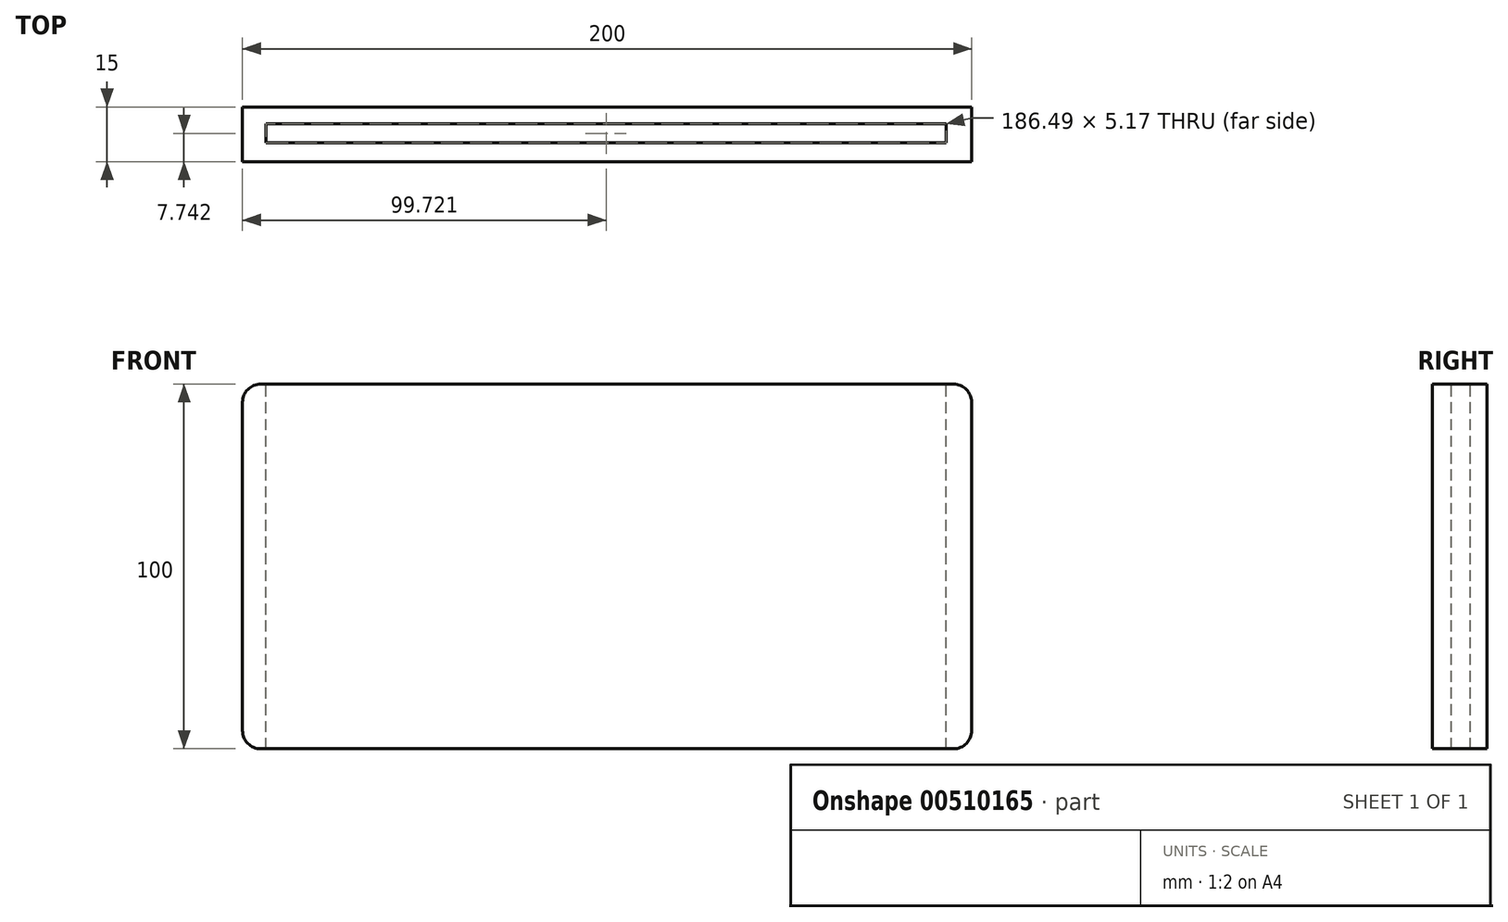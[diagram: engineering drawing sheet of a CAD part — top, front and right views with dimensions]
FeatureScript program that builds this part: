
annotation { "Feature Type Name" : "Feature", "Feature Type Description" : "" }
export const myFeature = defineFeature(function(context is Context, id is Id, definition is map)
    precondition{}
    {
        {
            var Q0;
            Q0=qCreatedBy(makeId("Front.planeOp"),FACE);
            var sketch = newSketch(context, id + "F0", { "sketchPlane" : qUnion([Q0])});
            skLineSegment(sketch, "E0.bottom", {"start": v(-99.03, -37.98) * mm, "end": v(100.97, -37.98) * mm});
            skLineSegment(sketch, "E0.top", {"start": v(-99.03, 62.02) * mm, "end": v(100.97, 62.02) * mm});
            skLineSegment(sketch, "E0.left", {"start": v(-99.03, -37.98) * mm, "end": v(-99.03, 62.02) * mm});
            skLineSegment(sketch, "E0.right", {"start": v(100.97, -37.98) * mm, "end": v(100.97, 62.02) * mm});
            skSolve(sketch);
        }
        {
            var Q0;
            Q0=makeQuery(id+"F0.imprint","IMPRINT",FACE,{"disambiguationData":[TD([[makeQuery(id+"F0.imprint","IMPRINT",EDGE,{"derivedFrom":sQuery(id+"F0.wireOp",EDGE,"E0.bottom")}),1.0]])]});
            extrude(context, id + "F1", {"entities" : qUnion([Q0]), "depth" : 15 * mm});
        }
        {
            var Q0;
            Q0=makeQuery(id+"F1.opExtrude","SWEPT_FACE",FACE,{"disambiguationData":[OSD([sQuery(id+"F0.wireOp",EDGE,"E0.bottom")])]});
            var sketch = newSketch(context, id + "F2", { "sketchPlane" : qUnion([Q0])});
            skLineSegment(sketch, "E1.bottom", {"start": v(-92.56, 9.84) * mm, "end": v(93.94, 9.84) * mm});
            skLineSegment(sketch, "E1.top", {"start": v(-92.56, 4.67) * mm, "end": v(93.94, 4.67) * mm});
            skLineSegment(sketch, "E1.left", {"start": v(-92.56, 9.84) * mm, "end": v(-92.56, 4.67) * mm});
            skLineSegment(sketch, "E1.right", {"start": v(93.94, 9.84) * mm, "end": v(93.94, 4.67) * mm});
            skSolve(sketch);
        }
        {
            var Q0;
            Q0=makeQuery(id+"F2.imprint","IMPRINT",FACE,{"disambiguationData":[TD([[makeQuery(id+"F2.imprint","IMPRINT",EDGE,{"derivedFrom":sQuery(id+"F2.wireOp",EDGE,"E1.bottom")}),-1.0]])]});
            extrude(context, id + "F3", {"entities" : qUnion([Q0]), "operationType" : NewBodyOperationType.REMOVE, "depth" : 25.4 * mm, "hasSecondDirection" : true, "secondDirectionOppositeDirection" : true, "secondDirectionDepth" : 187.42 * mm});
        }
        {
            var Q0;
            Q0=makeQuery(id+"F1.opExtrude","SWEPT_EDGE",EDGE,{"disambiguationData":[OSD([sQuery(id+"F0.wireOp",EDGE,"E0.top"),sQuery(id+"F0.wireOp",EDGE,"E0.left")])]});
            var Q1;
            Q1=makeQuery(id+"F1.opExtrude","SWEPT_EDGE",EDGE,{"disambiguationData":[OSD([sQuery(id+"F0.wireOp",EDGE,"E0.top"),sQuery(id+"F0.wireOp",EDGE,"E0.right")])]});
            var Q2;
            Q2=makeQuery(id+"F1.opExtrude","SWEPT_EDGE",EDGE,{"disambiguationData":[OSD([sQuery(id+"F0.wireOp",EDGE,"E0.bottom"),sQuery(id+"F0.wireOp",EDGE,"E0.right")])]});
            var Q3;
            Q3=makeQuery(id+"F1.opExtrude","SWEPT_EDGE",EDGE,{"disambiguationData":[OSD([sQuery(id+"F0.wireOp",EDGE,"E0.bottom"),sQuery(id+"F0.wireOp",EDGE,"E0.left")])]});
            fillet(context, id + "F4", {"entities" : qUnion([Q0, Q1, Q2, Q3]), "radius" : 5 * mm, "tangentPropagation" : true, "allowEdgeOverflow" : false});
        }
    });
